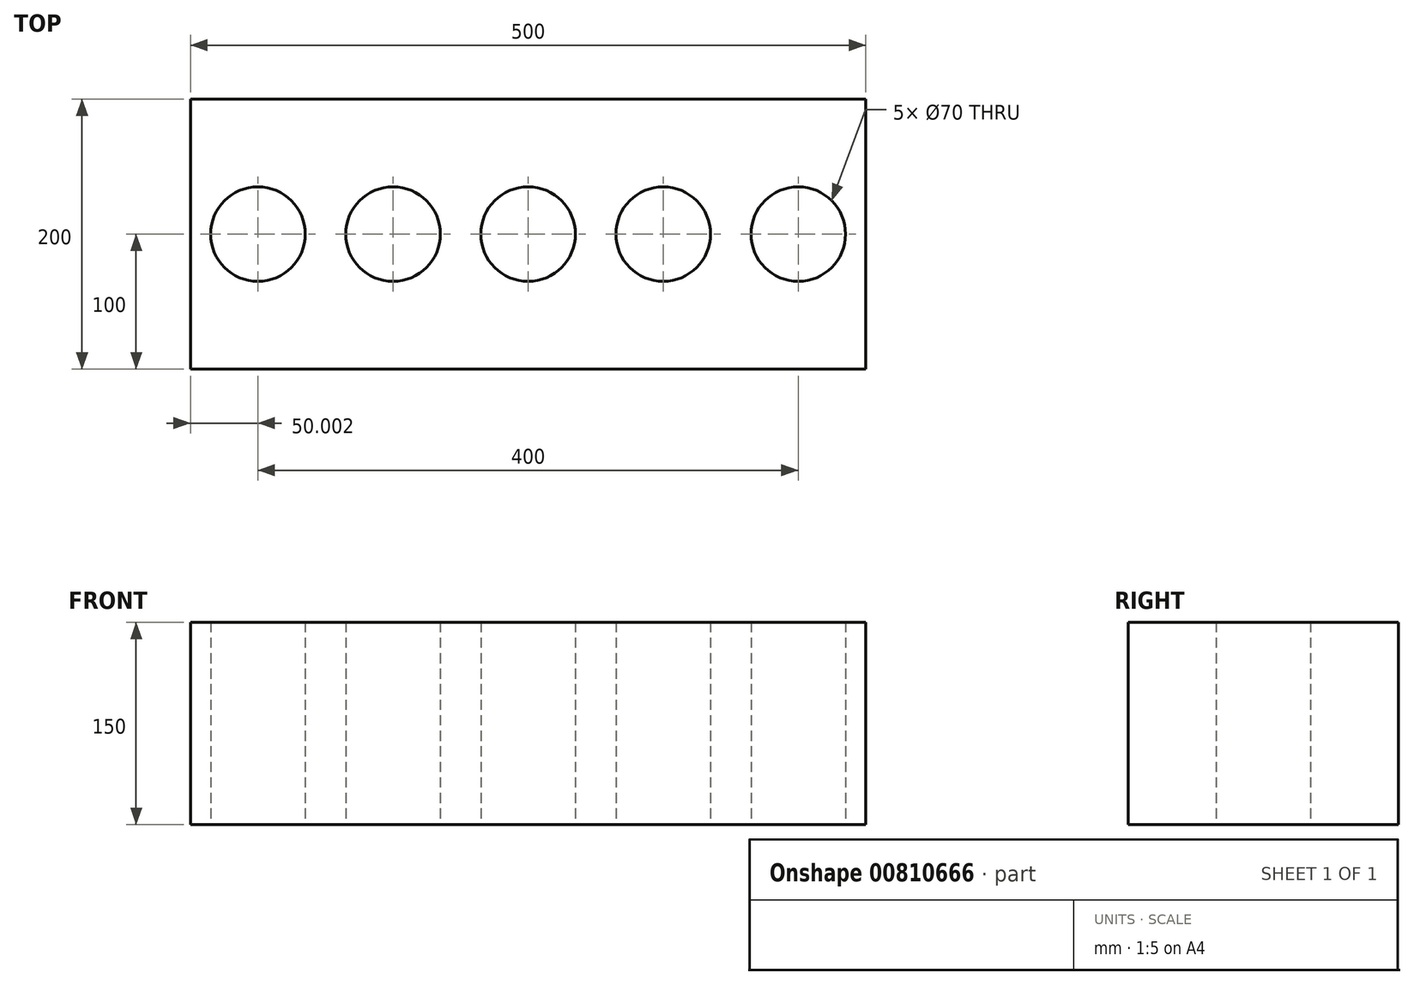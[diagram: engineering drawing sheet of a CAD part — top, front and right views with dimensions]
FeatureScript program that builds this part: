
annotation { "Feature Type Name" : "Feature", "Feature Type Description" : "" }
export const myFeature = defineFeature(function(context is Context, id is Id, definition is map)
    precondition{}
    {
        {
            var Q0;
            Q0=qCreatedBy(makeId("Top.planeOp"),FACE);
            var sketch = newSketch(context, id + "F0", { "sketchPlane" : qUnion([Q0])});
            skLineSegment(sketch, "E0.bottom", {"start": v(-381.97, -100) * mm, "end": v(118.03, -100) * mm});
            skLineSegment(sketch, "E0.top", {"start": v(-381.97, 100) * mm, "end": v(118.03, 100) * mm});
            skLineSegment(sketch, "E0.left", {"start": v(-381.97, -100) * mm, "end": v(-381.97, 100) * mm});
            skLineSegment(sketch, "E0.right", {"start": v(118.03, -100) * mm, "end": v(118.03, 100) * mm});
            skLineSegment(sketch, "E1", {"start": v(118.03, 0) * mm, "end": v(-381.97, 0) * mm});
            skCircle(sketch, "E2", {"center": v(68.03, 0) * mm, "radius": 35 * mm});
            skCircle(sketch, "E3.1.0.0", {"center": v(-31.97, 0) * mm, "radius": 35 * mm});
            skCircle(sketch, "E3.2.0.0", {"center": v(-131.97, 0) * mm, "radius": 35 * mm});
            skCircle(sketch, "E3.3.0.0", {"center": v(-231.97, 0) * mm, "radius": 35 * mm});
            skCircle(sketch, "E3.4.0.0", {"center": v(-331.97, 0) * mm, "radius": 35 * mm});
            skLineSegment(sketch, "E3.direction1", {"start": v(68.03, 0) * mm, "end": v(-31.97, 0) * mm});
            skSolve(sketch);
        }
        {
            var Q0;
            {var subQ10=sQuery(id+"F0.wireOp",EDGE,"E0.bottom");Q0=makeQuery(id+"F0.imprint","IMPRINT",FACE,{"disambiguationData":[TD([[makeQuery(id+"F0.imprint","IMPRINT",EDGE,{"derivedFrom":subQ10}),1.0]])]});}
            var Q1;
            {var subQ16=sQuery(id+"F0.wireOp",EDGE,"E0.top");Q1=makeQuery(id+"F0.imprint","IMPRINT",FACE,{"disambiguationData":[TD([[makeQuery(id+"F0.imprint","IMPRINT",EDGE,{"derivedFrom":subQ16}),-1.0]])]});}
            extrude(context, id + "F1", {"entities" : qUnion([Q0, Q1]), "depth" : 150 * mm, "offsetDistance" : 25 * mm});
        }
    });
